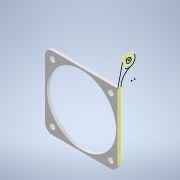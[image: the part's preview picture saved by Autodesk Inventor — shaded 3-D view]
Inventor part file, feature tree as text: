
AUTODESK INVENTOR PART (.ipt)
format: ipt  version: 2022 (Build 260153070, 153G)  size: 339,968 bytes
history: native  units: mm
features: other x4, extrude x3, sketch x3, reference x3, fillet x2
ambient origin geometry x8: Origin, YZ Plane, XZ Plane, XY Plane, X Axis, Y Axis, Z Axis, Center Point
bodies: Solid1 (feature_tree)
feature tree (15):
  extrude  "Extrusion1"  Depth=40.0mm
  extrude  "Extrusion2"  Depth=4.0mm
  fillet  "Fillet1"  Radius=4.0mm
  fillet  "Fillet2"  Radius=4.0mm
  extrude  "Extrusion3"  Depth=8.0mm
  sketch  "Sketch1"  dims[d0=40.0mm d1=40.0mm]
  sketch  "Sketch3"  dims[d2=4.0mm d3=4.0mm d4=4.0mm d5=4.0mm]
  reference  "Reference1"
  reference  "Reference2"
  sketch  "Sketch4"  dims[d6=38.0mm d7=8.0mm d8=14.0mm d9=3.0mm d10=1.6mm d11=0.0mm d15=2.7mm d16=4.1mm d17=2.8mm d18=0.0mm d19=0.0mm d20=40.0mm d21=7.25mm d22=1.6mm d23=0.0mm]
  reference  "Reference3"
  other  "<userpath> laptop\Desktop\Another3dPrinterShroud\MODELS\ENDER 3 ASSEMBLY.iam"
  other  "ENDER 3 ASSEMBLY.iam"
  other  "5015 RADIAL FAN:2"
  other  "FRONTPLATE:1"
